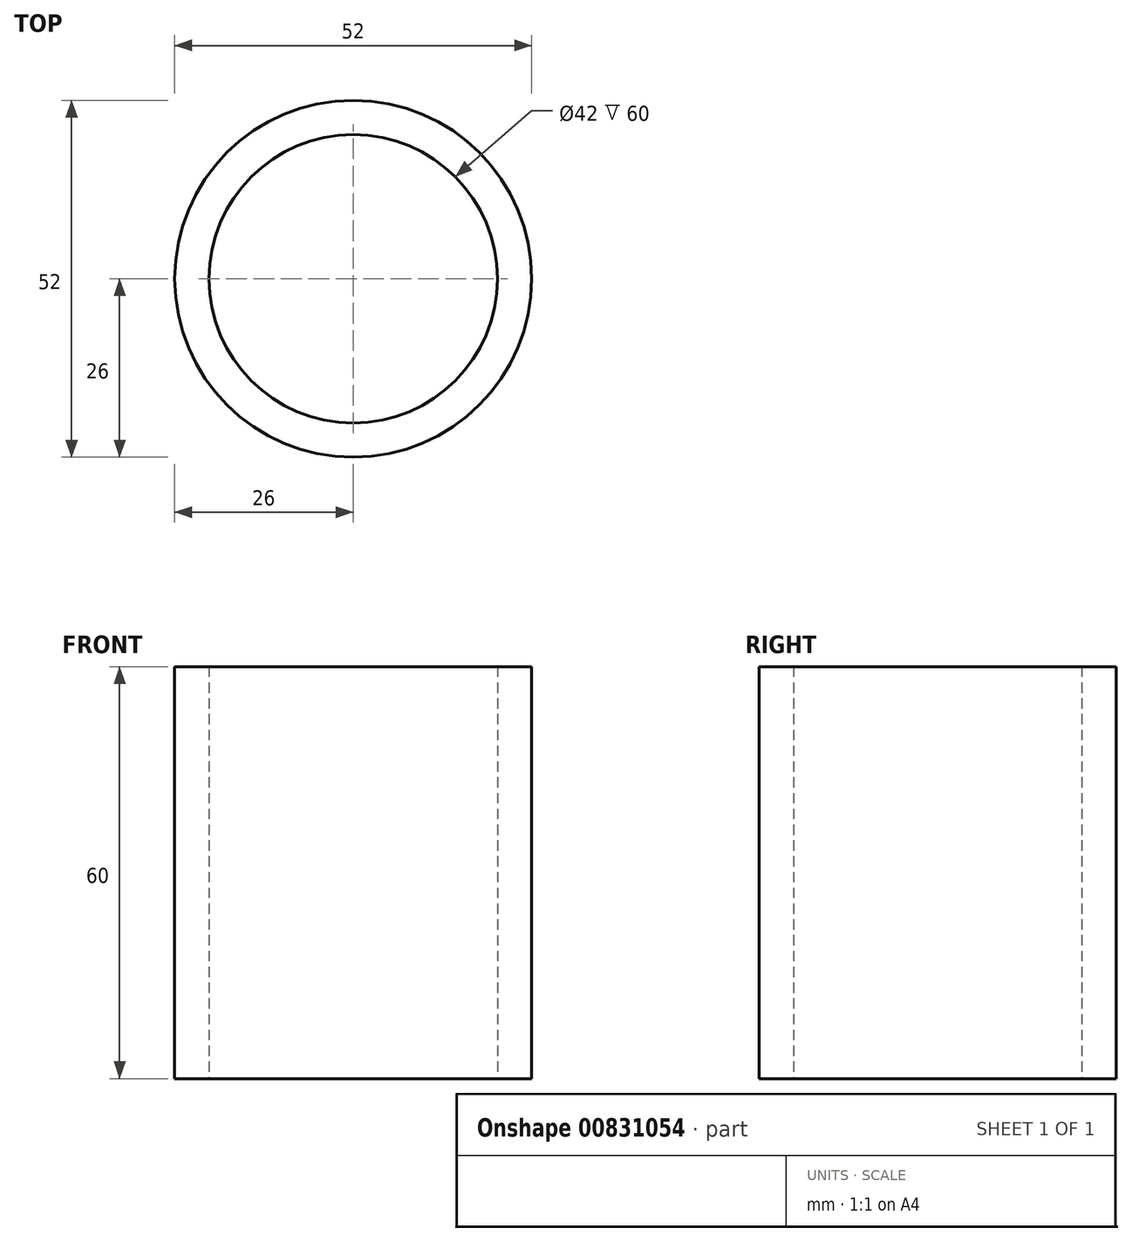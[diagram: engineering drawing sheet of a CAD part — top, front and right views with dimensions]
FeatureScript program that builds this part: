
annotation { "Feature Type Name" : "Feature", "Feature Type Description" : "" }
export const myFeature = defineFeature(function(context is Context, id is Id, definition is map)
    precondition{}
    {
        {
            var Q0;
            Q0=qCreatedBy(makeId("Top.planeOp"),FACE);
            var sketch = newSketch(context, id + "F0", { "sketchPlane" : qUnion([Q0])});
            skCircle(sketch, "E0", {"center": v(0, 0) * mm, "radius": 21 * mm});
            skCircle(sketch, "E1", {"center": v(0, 0) * mm, "radius": 26 * mm});
            skSolve(sketch);
        }
        {
            var Q0;
            Q0=makeQuery(id+"F0.imprint","IMPRINT",FACE,{"disambiguationData":[TD([[makeQuery(id+"F0.imprint","IMPRINT",EDGE,{"derivedFrom":sQuery(id+"F0.wireOp",EDGE,"E0")}),-1.0]])]});
            extrude(context, id + "F1", {"entities" : qUnion([Q0]), "depth" : 60 * mm, "offsetDistance" : 25 * mm});
        }
    });
